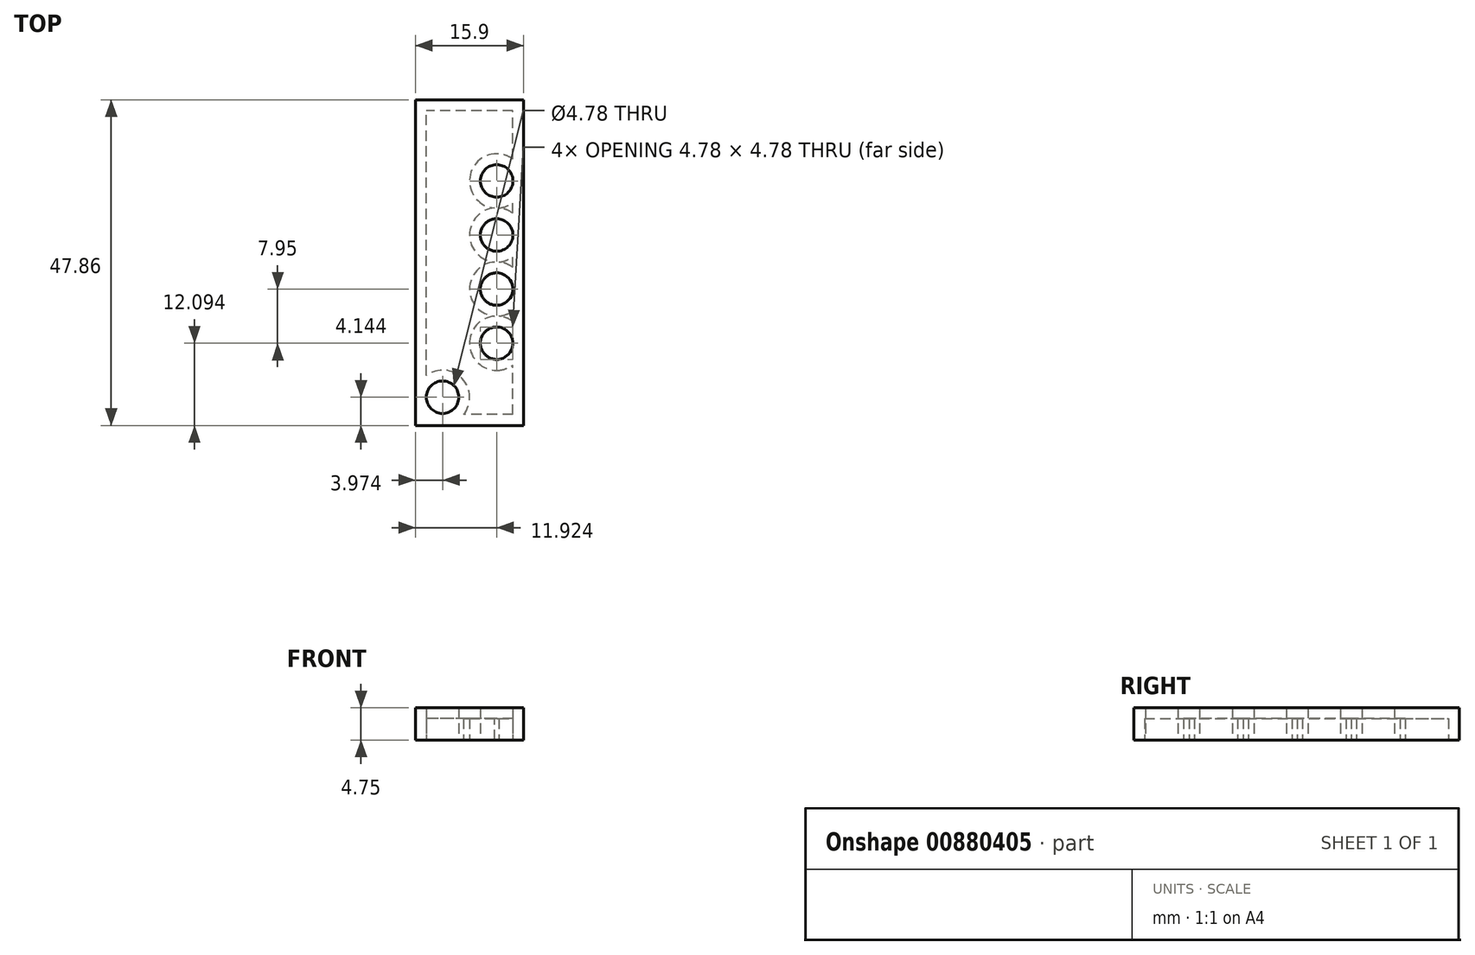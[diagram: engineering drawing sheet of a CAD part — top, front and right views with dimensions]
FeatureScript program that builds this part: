
annotation { "Feature Type Name" : "Feature", "Feature Type Description" : "" }
export const myFeature = defineFeature(function(context is Context, id is Id, definition is map)
    precondition{}
    {
        {
            var Q0;
            Q0=qCreatedBy(makeId("Top.planeOp"),FACE);
            var sketch = newSketch(context, id + "F0", { "sketchPlane" : qUnion([Q0])});
            skLineSegment(sketch, "E0.bottom", {"start": v(9.68, -35.75) * mm, "end": v(-6.22, -35.75) * mm});
            skLineSegment(sketch, "E0.top", {"start": v(9.68, 12.1) * mm, "end": v(-6.22, 12.1) * mm});
            skLineSegment(sketch, "E0.left", {"start": v(9.68, -35.75) * mm, "end": v(9.68, 12.1) * mm});
            skLineSegment(sketch, "E0.right", {"start": v(-6.22, -35.75) * mm, "end": v(-6.22, 12.1) * mm});
            skLineSegment(sketch, "E1", {"start": v(1.73, 12.1) * mm, "end": v(1.73, -35.75) * mm, "construction": true});
            skLineSegment(sketch, "E2", {"start": v(1.73, 12.1) * mm, "end": v(9.68, 12.1) * mm, "construction": true});
            skLineSegment(sketch, "E3", {"start": v(1.73, -35.75) * mm, "end": v(9.68, -35.75) * mm, "construction": true});
            skLineSegment(sketch, "E4", {"start": v(5.7, 12.1) * mm, "end": v(5.7, -35.75) * mm});
            skLineSegment(sketch, "E5", {"start": v(1.73, 12.1) * mm, "end": v(-6.22, 12.1) * mm});
            skLineSegment(sketch, "E6", {"start": v(-6.22, -35.75) * mm, "end": v(1.73, -35.75) * mm});
            skLineSegment(sketch, "E7", {"start": v(-2.25, -35.75) * mm, "end": v(-2.25, 12.1) * mm});
            skCircle(sketch, "E8", {"center": v(5.7, 8.14) * mm, "radius": 2.39 * mm});
            skCircle(sketch, "E9.1.0.0", {"center": v(5.7, 0.2) * mm, "radius": 2.39 * mm});
            skCircle(sketch, "E9.2.0.0", {"center": v(5.7, -7.76) * mm, "radius": 2.39 * mm});
            skCircle(sketch, "E9.3.0.0", {"center": v(5.7, -15.7) * mm, "radius": 2.39 * mm});
            skCircle(sketch, "E9.4.0.0", {"center": v(5.7, -23.66) * mm, "radius": 2.39 * mm});
            skCircle(sketch, "E9.5.0.0", {"center": v(5.7, -31.6) * mm, "radius": 2.39 * mm});
            skLineSegment(sketch, "E9.direction1", {"start": v(5.7, 8.14) * mm, "end": v(5.7, 0.2) * mm, "construction": true});
            skCircle(sketch, "E10.MirrorC", {"center": v(-2.25, 8.14) * mm, "radius": 2.39 * mm});
            skCircle(sketch, "E11.MirrorC", {"center": v(-2.25, 0.2) * mm, "radius": 2.39 * mm});
            skCircle(sketch, "E12.MirrorC", {"center": v(-2.25, -7.76) * mm, "radius": 2.39 * mm});
            skCircle(sketch, "E13.MirrorC", {"center": v(-2.25, -15.7) * mm, "radius": 2.39 * mm});
            skCircle(sketch, "E14.MirrorC", {"center": v(-2.25, -23.66) * mm, "radius": 2.39 * mm});
            skCircle(sketch, "E15.MirrorC", {"center": v(-2.25, -31.6) * mm, "radius": 2.39 * mm});
            skSolve(sketch);
        }
        {
            var Q0;
            {var subQ21=sQuery(id+"F0.wireOp",EDGE,"E0.left");Q0=makeQuery(id+"F0.imprint","IMPRINT",FACE,{"disambiguationData":[TD([[makeQuery(id+"F0.imprint","IMPRINT",EDGE,{"derivedFrom":subQ21}),1.0]])]});}
            var Q1;
            {var subQ18=sQuery(id+"F0.wireOp",EDGE,"E6");var subQ21=sQuery(id+"F0.wireOp",EDGE,"E0.bottom");var subQ22=makeQuery(id+"F0.imprint","INTERSECT",VERTEX,{"derivedFrom":[subQ21,subQ18]});Q1=makeQuery(id+"F0.imprint","IMPRINT",FACE,{"disambiguationData":[TD([[makeQuery(id+"F0.imprint","IMPRINT",EDGE,{"disambiguationData":[TD([[subQ22,1.0]])],"derivedFrom":subQ21}),-1.0]])]});}
            var Q2;
            {var subQ18=sQuery(id+"F0.wireOp",EDGE,"E0.right");Q2=makeQuery(id+"F0.imprint","IMPRINT",FACE,{"disambiguationData":[TD([[makeQuery(id+"F0.imprint","IMPRINT",EDGE,{"derivedFrom":subQ18}),-1.0]])]});}
            extrude(context, id + "F1", {"entities" : qUnion([Q0, Q1, Q2]), "depth" : 3.17 * mm, "offsetDistance" : 25.4 * mm});
        }
        {
            var Q0;
            {var subQ0=sQuery(id+"F0.wireOp",EDGE,"E15.MirrorC");var subQ1=sQuery(id+"F0.wireOp",EDGE,"E7");var subQ2=makeQuery(id+"F0.imprint","INTERSECT",VERTEX,{"disambiguationData":[OD(0.0)],"derivedFrom":[subQ1,subQ0]});Q0=makeQuery(id+"F0.imprint","IMPRINT",FACE,{"disambiguationData":[TD([[makeQuery(id+"F0.imprint","IMPRINT",EDGE,{"disambiguationData":[TD([[subQ2,-1.0]])],"derivedFrom":subQ1}),1.0]])]});}
            var Q1;
            {var subQ0=sQuery(id+"F0.wireOp",EDGE,"E15.MirrorC");var subQ1=sQuery(id+"F0.wireOp",EDGE,"E7");var subQ2=makeQuery(id+"F0.imprint","INTERSECT",VERTEX,{"disambiguationData":[OD(0.0)],"derivedFrom":[subQ1,subQ0]});Q1=makeQuery(id+"F0.imprint","IMPRINT",FACE,{"disambiguationData":[TD([[makeQuery(id+"F0.imprint","IMPRINT",EDGE,{"disambiguationData":[TD([[subQ2,-1.0]])],"derivedFrom":subQ1}),-1.0]])]});}
            var Q2;
            {var subQ0=sQuery(id+"F0.wireOp",EDGE,"E14.MirrorC");var subQ1=sQuery(id+"F0.wireOp",EDGE,"E7");var subQ2=makeQuery(id+"F0.imprint","INTERSECT",VERTEX,{"disambiguationData":[OD(0.0)],"derivedFrom":[subQ1,subQ0]});Q2=makeQuery(id+"F0.imprint","IMPRINT",FACE,{"disambiguationData":[TD([[makeQuery(id+"F0.imprint","IMPRINT",EDGE,{"disambiguationData":[TD([[subQ2,-1.0]])],"derivedFrom":subQ1}),1.0]])]});}
            var Q3;
            {var subQ0=sQuery(id+"F0.wireOp",EDGE,"E14.MirrorC");var subQ1=sQuery(id+"F0.wireOp",EDGE,"E7");var subQ2=makeQuery(id+"F0.imprint","INTERSECT",VERTEX,{"disambiguationData":[OD(0.0)],"derivedFrom":[subQ1,subQ0]});Q3=makeQuery(id+"F0.imprint","IMPRINT",FACE,{"disambiguationData":[TD([[makeQuery(id+"F0.imprint","IMPRINT",EDGE,{"disambiguationData":[TD([[subQ2,-1.0]])],"derivedFrom":subQ1}),-1.0]])]});}
            var Q4;
            {var subQ0=sQuery(id+"F0.wireOp",EDGE,"E13.MirrorC");var subQ1=sQuery(id+"F0.wireOp",EDGE,"E7");var subQ2=makeQuery(id+"F0.imprint","INTERSECT",VERTEX,{"disambiguationData":[OD(0.0)],"derivedFrom":[subQ1,subQ0]});Q4=makeQuery(id+"F0.imprint","IMPRINT",FACE,{"disambiguationData":[TD([[makeQuery(id+"F0.imprint","IMPRINT",EDGE,{"disambiguationData":[TD([[subQ2,-1.0]])],"derivedFrom":subQ1}),1.0]])]});}
            var Q5;
            {var subQ0=sQuery(id+"F0.wireOp",EDGE,"E13.MirrorC");var subQ1=sQuery(id+"F0.wireOp",EDGE,"E7");var subQ2=makeQuery(id+"F0.imprint","INTERSECT",VERTEX,{"disambiguationData":[OD(0.0)],"derivedFrom":[subQ1,subQ0]});Q5=makeQuery(id+"F0.imprint","IMPRINT",FACE,{"disambiguationData":[TD([[makeQuery(id+"F0.imprint","IMPRINT",EDGE,{"disambiguationData":[TD([[subQ2,-1.0]])],"derivedFrom":subQ1}),-1.0]])]});}
            var Q6;
            {var subQ0=sQuery(id+"F0.wireOp",EDGE,"E12.MirrorC");var subQ1=sQuery(id+"F0.wireOp",EDGE,"E7");var subQ2=makeQuery(id+"F0.imprint","INTERSECT",VERTEX,{"disambiguationData":[OD(0.0)],"derivedFrom":[subQ1,subQ0]});Q6=makeQuery(id+"F0.imprint","IMPRINT",FACE,{"disambiguationData":[TD([[makeQuery(id+"F0.imprint","IMPRINT",EDGE,{"disambiguationData":[TD([[subQ2,-1.0]])],"derivedFrom":subQ1}),1.0]])]});}
            var Q7;
            {var subQ0=sQuery(id+"F0.wireOp",EDGE,"E12.MirrorC");var subQ1=sQuery(id+"F0.wireOp",EDGE,"E7");var subQ2=makeQuery(id+"F0.imprint","INTERSECT",VERTEX,{"disambiguationData":[OD(0.0)],"derivedFrom":[subQ1,subQ0]});Q7=makeQuery(id+"F0.imprint","IMPRINT",FACE,{"disambiguationData":[TD([[makeQuery(id+"F0.imprint","IMPRINT",EDGE,{"disambiguationData":[TD([[subQ2,-1.0]])],"derivedFrom":subQ1}),-1.0]])]});}
            var Q8;
            {var subQ0=sQuery(id+"F0.wireOp",EDGE,"E11.MirrorC");var subQ1=sQuery(id+"F0.wireOp",EDGE,"E7");var subQ2=makeQuery(id+"F0.imprint","INTERSECT",VERTEX,{"disambiguationData":[OD(0.0)],"derivedFrom":[subQ1,subQ0]});Q8=makeQuery(id+"F0.imprint","IMPRINT",FACE,{"disambiguationData":[TD([[makeQuery(id+"F0.imprint","IMPRINT",EDGE,{"disambiguationData":[TD([[subQ2,-1.0]])],"derivedFrom":subQ1}),1.0]])]});}
            var Q9;
            {var subQ0=sQuery(id+"F0.wireOp",EDGE,"E11.MirrorC");var subQ1=sQuery(id+"F0.wireOp",EDGE,"E7");var subQ2=makeQuery(id+"F0.imprint","INTERSECT",VERTEX,{"disambiguationData":[OD(0.0)],"derivedFrom":[subQ1,subQ0]});Q9=makeQuery(id+"F0.imprint","IMPRINT",FACE,{"disambiguationData":[TD([[makeQuery(id+"F0.imprint","IMPRINT",EDGE,{"disambiguationData":[TD([[subQ2,-1.0]])],"derivedFrom":subQ1}),-1.0]])]});}
            var Q10;
            {var subQ0=sQuery(id+"F0.wireOp",EDGE,"E10.MirrorC");var subQ1=sQuery(id+"F0.wireOp",EDGE,"E7");var subQ2=makeQuery(id+"F0.imprint","INTERSECT",VERTEX,{"disambiguationData":[OD(0.0)],"derivedFrom":[subQ1,subQ0]});Q10=makeQuery(id+"F0.imprint","IMPRINT",FACE,{"disambiguationData":[TD([[makeQuery(id+"F0.imprint","IMPRINT",EDGE,{"disambiguationData":[TD([[subQ2,-1.0]])],"derivedFrom":subQ1}),1.0]])]});}
            var Q11;
            {var subQ0=sQuery(id+"F0.wireOp",EDGE,"E10.MirrorC");var subQ1=sQuery(id+"F0.wireOp",EDGE,"E7");var subQ2=makeQuery(id+"F0.imprint","INTERSECT",VERTEX,{"disambiguationData":[OD(0.0)],"derivedFrom":[subQ1,subQ0]});Q11=makeQuery(id+"F0.imprint","IMPRINT",FACE,{"disambiguationData":[TD([[makeQuery(id+"F0.imprint","IMPRINT",EDGE,{"disambiguationData":[TD([[subQ2,-1.0]])],"derivedFrom":subQ1}),-1.0]])]});}
            var Q12;
            {var subQ0=sQuery(id+"F0.wireOp",EDGE,"E9.5.0.0");var subQ1=sQuery(id+"F0.wireOp",EDGE,"E4");var subQ2=makeQuery(id+"F0.imprint","INTERSECT",VERTEX,{"disambiguationData":[OD(0.0)],"derivedFrom":[subQ1,subQ0]});Q12=makeQuery(id+"F0.imprint","IMPRINT",FACE,{"disambiguationData":[TD([[makeQuery(id+"F0.imprint","IMPRINT",EDGE,{"disambiguationData":[TD([[subQ2,-1.0]])],"derivedFrom":subQ1}),-1.0]])]});}
            var Q13;
            {var subQ0=sQuery(id+"F0.wireOp",EDGE,"E9.5.0.0");var subQ1=sQuery(id+"F0.wireOp",EDGE,"E4");var subQ2=makeQuery(id+"F0.imprint","INTERSECT",VERTEX,{"disambiguationData":[OD(0.0)],"derivedFrom":[subQ1,subQ0]});Q13=makeQuery(id+"F0.imprint","IMPRINT",FACE,{"disambiguationData":[TD([[makeQuery(id+"F0.imprint","IMPRINT",EDGE,{"disambiguationData":[TD([[subQ2,-1.0]])],"derivedFrom":subQ1}),1.0]])]});}
            var Q14;
            {var subQ0=sQuery(id+"F0.wireOp",EDGE,"E9.4.0.0");var subQ1=sQuery(id+"F0.wireOp",EDGE,"E4");var subQ2=makeQuery(id+"F0.imprint","INTERSECT",VERTEX,{"disambiguationData":[OD(0.0)],"derivedFrom":[subQ1,subQ0]});Q14=makeQuery(id+"F0.imprint","IMPRINT",FACE,{"disambiguationData":[TD([[makeQuery(id+"F0.imprint","IMPRINT",EDGE,{"disambiguationData":[TD([[subQ2,-1.0]])],"derivedFrom":subQ1}),-1.0]])]});}
            var Q15;
            {var subQ0=sQuery(id+"F0.wireOp",EDGE,"E9.4.0.0");var subQ1=sQuery(id+"F0.wireOp",EDGE,"E4");var subQ2=makeQuery(id+"F0.imprint","INTERSECT",VERTEX,{"disambiguationData":[OD(0.0)],"derivedFrom":[subQ1,subQ0]});Q15=makeQuery(id+"F0.imprint","IMPRINT",FACE,{"disambiguationData":[TD([[makeQuery(id+"F0.imprint","IMPRINT",EDGE,{"disambiguationData":[TD([[subQ2,-1.0]])],"derivedFrom":subQ1}),1.0]])]});}
            var Q16;
            {var subQ0=sQuery(id+"F0.wireOp",EDGE,"E9.3.0.0");var subQ1=sQuery(id+"F0.wireOp",EDGE,"E4");var subQ2=makeQuery(id+"F0.imprint","INTERSECT",VERTEX,{"disambiguationData":[OD(0.0)],"derivedFrom":[subQ1,subQ0]});Q16=makeQuery(id+"F0.imprint","IMPRINT",FACE,{"disambiguationData":[TD([[makeQuery(id+"F0.imprint","IMPRINT",EDGE,{"disambiguationData":[TD([[subQ2,-1.0]])],"derivedFrom":subQ1}),-1.0]])]});}
            var Q17;
            {var subQ0=sQuery(id+"F0.wireOp",EDGE,"E9.2.0.0");var subQ1=sQuery(id+"F0.wireOp",EDGE,"E4");var subQ2=makeQuery(id+"F0.imprint","INTERSECT",VERTEX,{"disambiguationData":[OD(0.0)],"derivedFrom":[subQ1,subQ0]});Q17=makeQuery(id+"F0.imprint","IMPRINT",FACE,{"disambiguationData":[TD([[makeQuery(id+"F0.imprint","IMPRINT",EDGE,{"disambiguationData":[TD([[subQ2,-1.0]])],"derivedFrom":subQ1}),-1.0]])]});}
            var Q18;
            {var subQ0=sQuery(id+"F0.wireOp",EDGE,"E9.2.0.0");var subQ1=sQuery(id+"F0.wireOp",EDGE,"E4");var subQ2=makeQuery(id+"F0.imprint","INTERSECT",VERTEX,{"disambiguationData":[OD(0.0)],"derivedFrom":[subQ1,subQ0]});Q18=makeQuery(id+"F0.imprint","IMPRINT",FACE,{"disambiguationData":[TD([[makeQuery(id+"F0.imprint","IMPRINT",EDGE,{"disambiguationData":[TD([[subQ2,-1.0]])],"derivedFrom":subQ1}),1.0]])]});}
            var Q19;
            {var subQ0=sQuery(id+"F0.wireOp",EDGE,"E9.3.0.0");var subQ1=sQuery(id+"F0.wireOp",EDGE,"E4");var subQ2=makeQuery(id+"F0.imprint","INTERSECT",VERTEX,{"disambiguationData":[OD(0.0)],"derivedFrom":[subQ1,subQ0]});Q19=makeQuery(id+"F0.imprint","IMPRINT",FACE,{"disambiguationData":[TD([[makeQuery(id+"F0.imprint","IMPRINT",EDGE,{"disambiguationData":[TD([[subQ2,-1.0]])],"derivedFrom":subQ1}),1.0]])]});}
            var Q20;
            {var subQ0=sQuery(id+"F0.wireOp",EDGE,"E9.1.0.0");var subQ1=sQuery(id+"F0.wireOp",EDGE,"E4");var subQ2=makeQuery(id+"F0.imprint","INTERSECT",VERTEX,{"disambiguationData":[OD(0.0)],"derivedFrom":[subQ1,subQ0]});Q20=makeQuery(id+"F0.imprint","IMPRINT",FACE,{"disambiguationData":[TD([[makeQuery(id+"F0.imprint","IMPRINT",EDGE,{"disambiguationData":[TD([[subQ2,-1.0]])],"derivedFrom":subQ1}),-1.0]])]});}
            var Q21;
            {var subQ0=sQuery(id+"F0.wireOp",EDGE,"E9.1.0.0");var subQ1=sQuery(id+"F0.wireOp",EDGE,"E4");var subQ2=makeQuery(id+"F0.imprint","INTERSECT",VERTEX,{"disambiguationData":[OD(0.0)],"derivedFrom":[subQ1,subQ0]});Q21=makeQuery(id+"F0.imprint","IMPRINT",FACE,{"disambiguationData":[TD([[makeQuery(id+"F0.imprint","IMPRINT",EDGE,{"disambiguationData":[TD([[subQ2,-1.0]])],"derivedFrom":subQ1}),1.0]])]});}
            var Q22;
            {var subQ0=sQuery(id+"F0.wireOp",EDGE,"E8");var subQ1=sQuery(id+"F0.wireOp",EDGE,"E4");var subQ2=makeQuery(id+"F0.imprint","INTERSECT",VERTEX,{"disambiguationData":[OD(0.0)],"derivedFrom":[subQ1,subQ0]});Q22=makeQuery(id+"F0.imprint","IMPRINT",FACE,{"disambiguationData":[TD([[makeQuery(id+"F0.imprint","IMPRINT",EDGE,{"disambiguationData":[TD([[subQ2,-1.0]])],"derivedFrom":subQ1}),-1.0]])]});}
            var Q23;
            {var subQ0=sQuery(id+"F0.wireOp",EDGE,"E8");var subQ1=sQuery(id+"F0.wireOp",EDGE,"E4");var subQ2=makeQuery(id+"F0.imprint","INTERSECT",VERTEX,{"disambiguationData":[OD(0.0)],"derivedFrom":[subQ1,subQ0]});Q23=makeQuery(id+"F0.imprint","IMPRINT",FACE,{"disambiguationData":[TD([[makeQuery(id+"F0.imprint","IMPRINT",EDGE,{"disambiguationData":[TD([[subQ2,-1.0]])],"derivedFrom":subQ1}),1.0]])]});}
            extrude(context, id + "F2", {"entities" : qUnion([Q0, Q1, Q2, Q3, Q4, Q5, Q6, Q7, Q8, Q9, Q10, Q11, Q12, Q13, Q14, Q15, Q16, Q17, Q18, Q19, Q20, Q21, Q22, Q23]), "operationType" : NewBodyOperationType.ADD, "depth" : 4.75 * mm, "offsetDistance" : 25.4 * mm});
        }
        {
            var Q0;
            {var subQ0=sQuery(id+"F0.wireOp",EDGE,"E15.MirrorC");var subQ1=sQuery(id+"F0.wireOp",EDGE,"E14.MirrorC");var subQ2=sQuery(id+"F0.wireOp",EDGE,"E13.MirrorC");var subQ3=sQuery(id+"F0.wireOp",EDGE,"E12.MirrorC");var subQ4=sQuery(id+"F0.wireOp",EDGE,"E11.MirrorC");var subQ5=sQuery(id+"F0.wireOp",EDGE,"E10.MirrorC");var subQ6=sQuery(id+"F0.wireOp",EDGE,"E9.5.0.0");var subQ7=sQuery(id+"F0.wireOp",EDGE,"E9.4.0.0");var subQ8=sQuery(id+"F0.wireOp",EDGE,"E9.3.0.0");var subQ9=sQuery(id+"F0.wireOp",EDGE,"E9.2.0.0");var subQ10=sQuery(id+"F0.wireOp",EDGE,"E9.1.0.0");var subQ11=sQuery(id+"F0.wireOp",EDGE,"E8");Q0=makeQuery(id+"F2.boolean.opBoolean","MERGE",FACE,{"derivedFrom":[makeQuery(id+"F1.opExtrude","CAP_FACE",FACE,{"disambiguationData":[OSD([sQuery(id+"F0.wireOp",EDGE,"E0.bottom"),sQuery(id+"F0.wireOp",EDGE,"E0.top"),sQuery(id+"F0.wireOp",EDGE,"E0.left"),sQuery(id+"F0.wireOp",EDGE,"E0.right"),sQuery(id+"F0.wireOp",EDGE,"E5"),sQuery(id+"F0.wireOp",EDGE,"E6"),subQ11,subQ10,subQ9,subQ8,subQ7,subQ6,subQ5,subQ4,subQ3,subQ2,subQ1,subQ0])],"isStart":true}),makeQuery(id+"F2.opExtrude","CAP_FACE",FACE,{"disambiguationData":[OSD([subQ11])],"isStart":true}),makeQuery(id+"F2.opExtrude","CAP_FACE",FACE,{"disambiguationData":[OSD([subQ10])],"isStart":true}),makeQuery(id+"F2.opExtrude","CAP_FACE",FACE,{"disambiguationData":[OSD([subQ9])],"isStart":true}),makeQuery(id+"F2.opExtrude","CAP_FACE",FACE,{"disambiguationData":[OSD([subQ8])],"isStart":true}),makeQuery(id+"F2.opExtrude","CAP_FACE",FACE,{"disambiguationData":[OSD([subQ7])],"isStart":true}),makeQuery(id+"F2.opExtrude","CAP_FACE",FACE,{"disambiguationData":[OSD([subQ6])],"isStart":true}),makeQuery(id+"F2.opExtrude","CAP_FACE",FACE,{"disambiguationData":[OSD([subQ5])],"isStart":true}),makeQuery(id+"F2.opExtrude","CAP_FACE",FACE,{"disambiguationData":[OSD([subQ4])],"isStart":true}),makeQuery(id+"F2.opExtrude","CAP_FACE",FACE,{"disambiguationData":[OSD([subQ3])],"isStart":true}),makeQuery(id+"F2.opExtrude","CAP_FACE",FACE,{"disambiguationData":[OSD([subQ2])],"isStart":true}),makeQuery(id+"F2.opExtrude","CAP_FACE",FACE,{"disambiguationData":[OSD([subQ1])],"isStart":true}),makeQuery(id+"F2.opExtrude","CAP_FACE",FACE,{"disambiguationData":[OSD([subQ0])],"isStart":true})]});}
            shell(context, id + "F3", {"entities" : qUnion([Q0]), "thickness" : 1.6 * mm});
        }
    });
